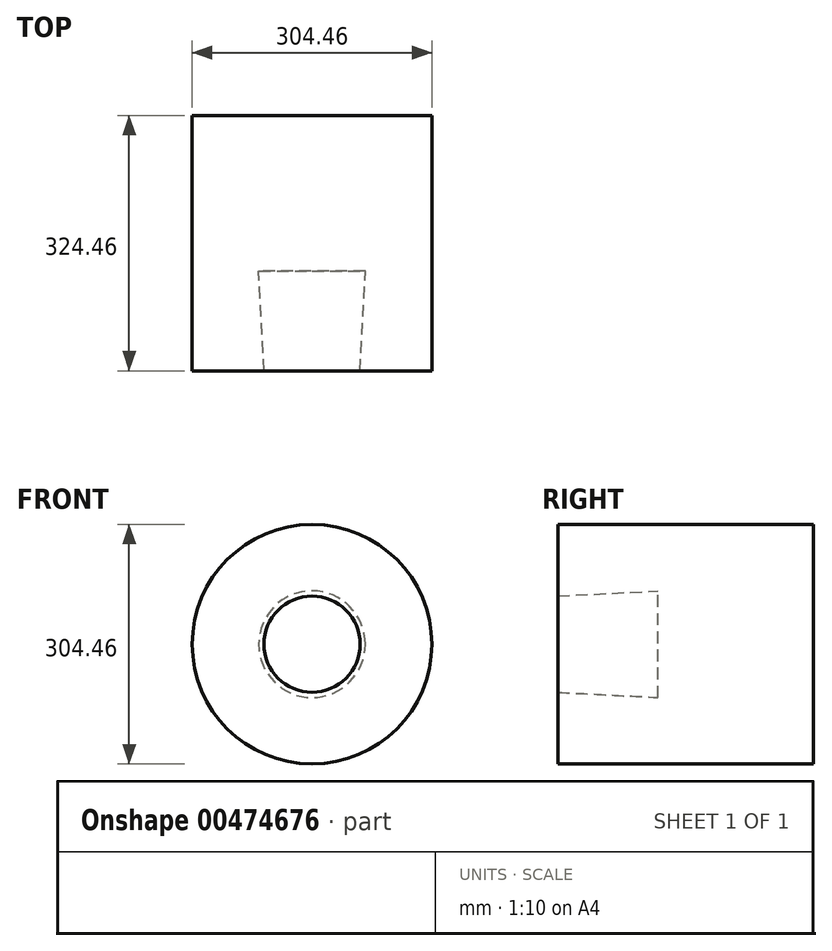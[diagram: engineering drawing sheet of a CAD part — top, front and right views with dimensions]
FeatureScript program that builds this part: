
annotation { "Feature Type Name" : "Feature", "Feature Type Description" : "" }
export const myFeature = defineFeature(function(context is Context, id is Id, definition is map)
    precondition{}
    {
        {
            var Q0;
            Q0=qCreatedBy(makeId("Front.planeOp"),FACE);
            var sketch = newSketch(context, id + "F0", { "sketchPlane" : qUnion([Q0])});
            skCircle(sketch, "E0", {"center": v(0, 0) * mm, "radius": 152.23 * mm});
            skSolve(sketch);
        }
        {
            var Q0;
            Q0=makeQuery(id+"F0.imprint","IMPRINT",FACE,{"disambiguationData":[TD([[makeQuery(id+"F0.imprint","IMPRINT",EDGE,{"derivedFrom":sQuery(id+"F0.wireOp",EDGE,"E0")}),1.0]])]});
            var Q1;
            Q1=sQuery(id+"F0.wireOp",EDGE,"E0");
            extrude(context, id + "F1", {"entities" : qUnion([Q0]), "surfaceEntities" : qUnion([Q1]), "depth" : 324.46 * mm});
        }
        {
            var Q0;
            Q0=makeQuery(id+"F1.opExtrude","CAP_FACE",FACE,{"disambiguationData":[OSD([sQuery(id+"F0.wireOp",EDGE,"E0")])],"isStart":false});
            var sketch = newSketch(context, id + "F2", { "sketchPlane" : qUnion([Q0])});
            skCircle(sketch, "E1", {"center": v(0, 0) * mm, "radius": 61.06 * mm});
            skSolve(sketch);
        }
        {
            var Q0;
            Q0 = qSketchRegion(id + "F2", true);
            extrude(context, id + "F3", {"entities" : qUnion([Q0]), "operationType" : NewBodyOperationType.REMOVE, "oppositeDirection" : true, "depth" : 127 * mm, "hasDraft" : true, "draftAngle" : 3 * degree});
        }
    });
